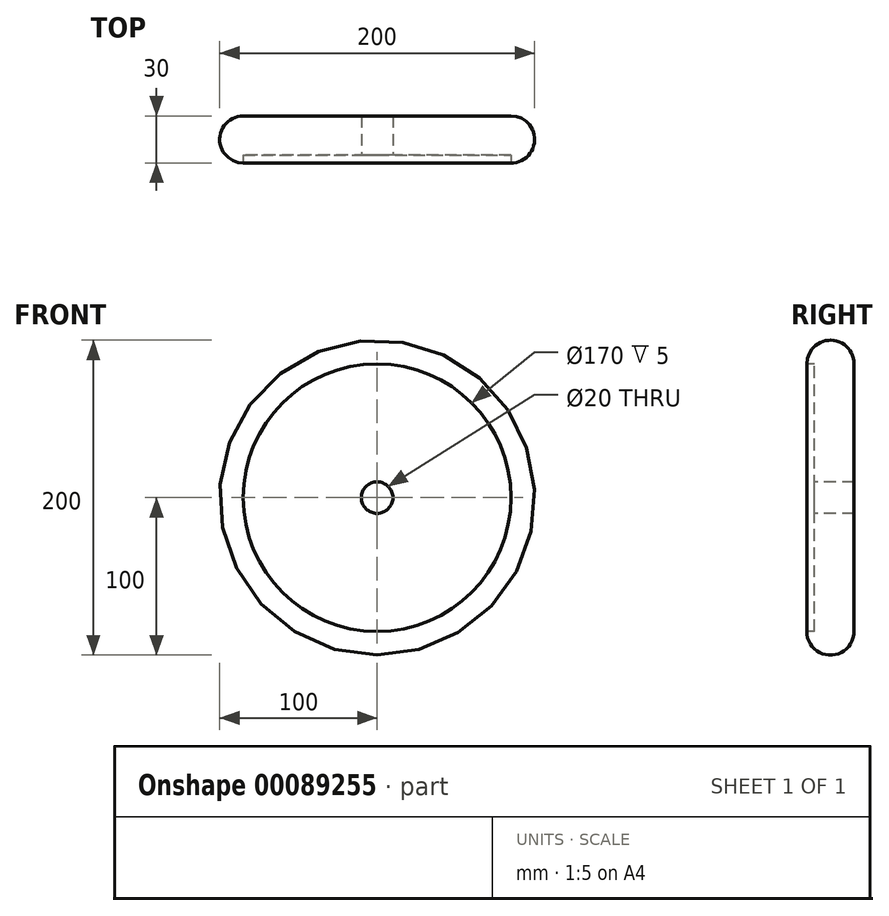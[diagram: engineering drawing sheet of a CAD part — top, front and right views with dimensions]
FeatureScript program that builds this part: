
annotation { "Feature Type Name" : "Feature", "Feature Type Description" : "" }
export const myFeature = defineFeature(function(context is Context, id is Id, definition is map)
    precondition{}
    {
        {
            var Q0;
            Q0=qCreatedBy(makeId("Front.planeOp"),FACE);
            var sketch = newSketch(context, id + "F0", { "sketchPlane" : qUnion([Q0])});
            skCircle(sketch, "E0", {"center": v(0, 0) * mm, "radius": 100 * mm});
            skSolve(sketch);
        }
        {
            var Q0;
            Q0=makeQuery(id+"F0.imprint","IMPRINT",FACE,{"disambiguationData":[TD([[makeQuery(id+"F0.imprint","IMPRINT",EDGE,{"derivedFrom":sQuery(id+"F0.wireOp",EDGE,"E0")}),1.0]])]});
            extrude(context, id + "F1", {"entities" : qUnion([Q0]), "depth" : 30 * mm});
        }
        {
            var Q0;
            Q0=makeQuery(id+"F1.opExtrude","CAP_EDGE",EDGE,{"disambiguationData":[OSD([sQuery(id+"F0.wireOp",EDGE,"E0")])],"isStart":false});
            var Q1;
            Q1=makeQuery(id+"F1.opExtrude","CAP_EDGE",EDGE,{"disambiguationData":[OSD([sQuery(id+"F0.wireOp",EDGE,"E0")])],"isStart":true});
            fillet(context, id + "F2", {"entities" : qUnion([Q0, Q1]), "radius" : 15 * mm, "tangentPropagation" : true, "allowEdgeOverflow" : false});
        }
        {
            var Q0;
            Q0=makeQuery(id+"F1.opExtrude","CAP_FACE",FACE,{"disambiguationData":[OSD([sQuery(id+"F0.wireOp",EDGE,"E0")])],"isStart":false});
            extrude(context, id + "F3", {"entities" : qUnion([Q0]), "operationType" : NewBodyOperationType.REMOVE, "oppositeDirection" : true, "depth" : 5 * mm});
        }
        {
            var Q0;
            Q0=makeQuery(id+"F3.boolean.opBoolean","COPY",FACE,{"derivedFrom":makeQuery(id+"F3.opExtrude","CAP_FACE",FACE,{"disambiguationData":[OSD([sQuery(id+"F0.wireOp",EDGE,"E0")])],"isStart":false})});
            var sketch = newSketch(context, id + "F4", { "sketchPlane" : qUnion([Q0])});
            skCircle(sketch, "E1", {"center": v(0, 0) * mm, "radius": 10 * mm});
            skSolve(sketch);
        }
        {
            var Q0;
            Q0=makeQuery(id+"F4.imprint","IMPRINT",FACE,{"disambiguationData":[TD([[makeQuery(id+"F4.imprint","IMPRINT",EDGE,{"derivedFrom":sQuery(id+"F4.wireOp",EDGE,"E1")}),1.0]])]});
            extrude(context, id + "F5", {"entities" : qUnion([Q0]), "operationType" : NewBodyOperationType.REMOVE, "endBound" : BoundingType.THROUGH_ALL, "oppositeDirection" : true, "depth" : 25 * mm});
        }
    });
